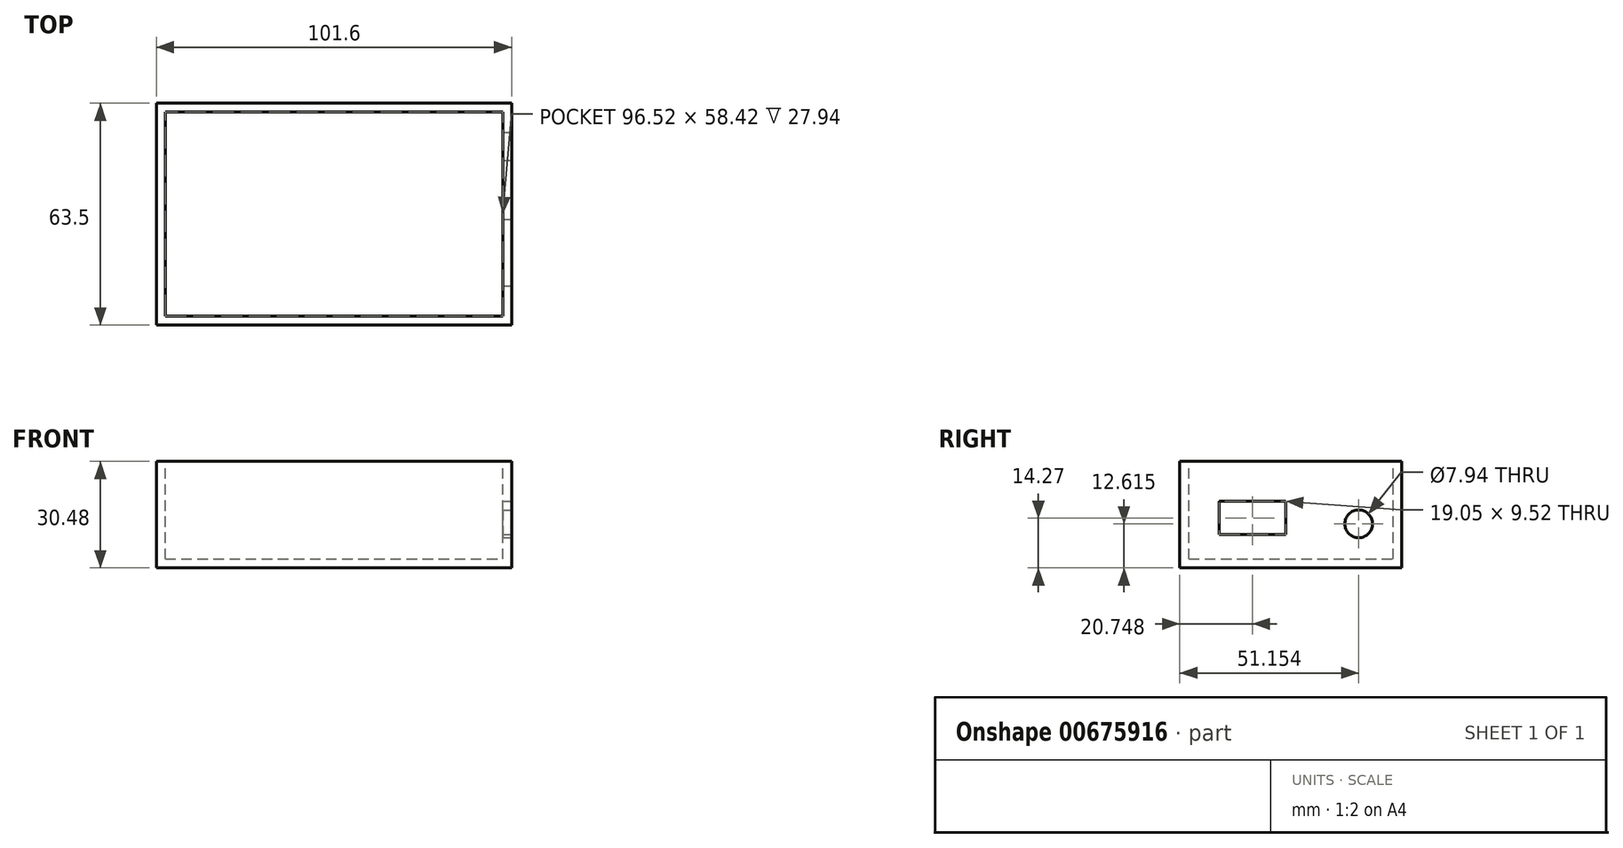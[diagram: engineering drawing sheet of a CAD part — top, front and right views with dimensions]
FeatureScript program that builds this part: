
annotation { "Feature Type Name" : "Feature", "Feature Type Description" : "" }
export const myFeature = defineFeature(function(context is Context, id is Id, definition is map)
    precondition{}
    {
        {
            var Q0;
            Q0=qCreatedBy(makeId("Front.planeOp"),FACE);
            var sketch = newSketch(context, id + "F0", { "sketchPlane" : qUnion([Q0])});
            skLineSegment(sketch, "E0.bottom", {"start": v(0, 0) * mm, "end": v(101.6, 0) * mm});
            skLineSegment(sketch, "E0.top", {"start": v(0, 30.48) * mm, "end": v(101.6, 30.48) * mm});
            skLineSegment(sketch, "E0.left", {"start": v(0, 0) * mm, "end": v(0, 30.48) * mm});
            skLineSegment(sketch, "E0.right", {"start": v(101.6, 0) * mm, "end": v(101.6, 30.48) * mm});
            skSolve(sketch);
        }
        {
            var Q0;
            Q0=makeQuery(id+"F0.imprint","IMPRINT",FACE,{"disambiguationData":[TD([[makeQuery(id+"F0.imprint","IMPRINT",EDGE,{"derivedFrom":sQuery(id+"F0.wireOp",EDGE,"E0.bottom")}),1.0]])]});
            extrude(context, id + "F1", {"entities" : qUnion([Q0]), "depth" : 63.5 * mm, "offsetDistance" : 25.4 * mm});
        }
        {
            var Q0;
            Q0=makeQuery(id+"F1.opExtrude","SWEPT_FACE",FACE,{"disambiguationData":[OSD([sQuery(id+"F0.wireOp",EDGE,"E0.top")])]});
            shell(context, id + "F2", {"entities" : qUnion([Q0]), "thickness" : 2.54 * mm});
        }
        {
            var Q0;
            Q0=makeQuery(id+"F1.opExtrude","SWEPT_FACE",FACE,{"disambiguationData":[OSD([sQuery(id+"F0.wireOp",EDGE,"E0.right")])]});
            var sketch = newSketch(context, id + "F3", { "sketchPlane" : qUnion([Q0])});
            skPoint(sketch, "E1", {"position": v(0, 12.61) * mm});
            skPoint(sketch, "E2", {"position": v(-12.35, 0) * mm});
            skPoint(sketch, "E3", {"position": v(-12.35, 12.61) * mm});
            skSolve(sketch);
        }
        {
            var Q0;
            Q0=sQuery(id+"F3.wireOp",VERTEX,"E3");
            var Q1;
            Q1=makeQuery(id+"F1.opExtrude","SWEPT_BODY",BODY,{"disambiguationData":[OSD([sQuery(id+"F0.wireOp",EDGE,"E0.bottom"),sQuery(id+"F0.wireOp",EDGE,"E0.top"),sQuery(id+"F0.wireOp",EDGE,"E0.left"),sQuery(id+"F0.wireOp",EDGE,"E0.right")])]});
            hole(context, id + "F4", {"style" : HoleStyle.SIMPLE, "endStyle" : HoleEndStyle.BLIND, "holeDiameter" : 7.94 * mm, "majorDiameter" : 6.35 * mm, "holeDepth" : 12.7 * mm, "isTappedThrough" : true, "tappedDepth" : 12.7 * mm, "tapClearance" : 3, "locations" : qUnion([Q0]), "scope" : qUnion([Q1])});
        }
        {
            var Q0;
            Q0=makeQuery(id+"F1.opExtrude","SWEPT_FACE",FACE,{"disambiguationData":[OSD([sQuery(id+"F0.wireOp",EDGE,"E0.right")])]});
            var sketch = newSketch(context, id + "F5", { "sketchPlane" : qUnion([Q0])});
            skLineSegment(sketch, "E4.bottom", {"start": v(-52.28, 19.03) * mm, "end": v(-33.23, 19.03) * mm});
            skLineSegment(sketch, "E4.top", {"start": v(-52.28, 9.5) * mm, "end": v(-33.23, 9.5) * mm});
            skLineSegment(sketch, "E4.left", {"start": v(-52.28, 19.03) * mm, "end": v(-52.28, 9.5) * mm});
            skLineSegment(sketch, "E4.right", {"start": v(-33.23, 19.03) * mm, "end": v(-33.23, 9.5) * mm});
            skSolve(sketch);
        }
        {
            var Q0;
            Q0=makeQuery(id+"F5.imprint","IMPRINT",FACE,{"disambiguationData":[TD([[makeQuery(id+"F5.imprint","IMPRINT",EDGE,{"derivedFrom":sQuery(id+"F5.wireOp",EDGE,"E4.bottom")}),-1.0]])]});
            extrude(context, id + "F6", {"entities" : qUnion([Q0]), "operationType" : NewBodyOperationType.REMOVE, "oppositeDirection" : true, "depth" : 25.4 * mm, "offsetDistance" : 25.4 * mm});
        }
    });
